# Revit family: NBS_DuPontCorian_CounterTopWashBasins_CorianSingleSink966
name_source: partatom
category: Plumbing Fixtures
revit_build: Autodesk Revit 2014 (Build: 20130709_2115(x64)
units: mm (PartAtom-declared; Revit-internal decimal feet)

## types (1)
- CorianSingleSink966
    AssetType = Fixed
    BIMObjectName = NBS_DuPontCorian_CounterTopWashBasins_CorianSingleSink966
    ColourOptions = Bone, Cameo White, Designer White, Glacier White, Vanilla
    Default Elevation = 0 mm  [stored 0 ft]
    Description = The extraordinary versatility of DuPont™ Corian® makes it the right choice for bathrooms. Bathroom basins made with Corian® combine beauty, functionality, durability and stain resistance with easy care and the abundant design and colour options that make all the difference.
    DrainSize = 0 mm  [stored 0 ft]
    DurationUnit = year
    Features = Designed to be integrated into a Corian® worksurface. Available in full colour range as Standard or bespoke colours. Hygienic.
    Finish = Semi gloss
    Form = Inset countertop or Mounted under countertop (undermount)
    IfcExportAs = IfcSanitaryTerminalType
    IfcExportType = WASHHANDBASIN
    IntegralAccessories = Includes overflow piece and 25mm diameter overflow elbow
    InternalDepth = 176 mm
    InternalLength = 700 mm
    InternalWidth = 401 mm
    Manufacturer = DuPont™ Corian®
    ManufacturerName = DuPont Corian
    ManufacturerURL = www.corian.co.uk
    Material = ±⅓ acrylic resin (also known as polymethyl methacrylate or PMMA) and ±⅔ aluminium trihydrate natural minerals
    ModelNumber = 966
    ModelReference = Corian® Single Sink
    MountingOptions = Undermount classical, Undermount seamless
    NBSCertification = http://www.nationalbimlibrary.com
    NBSDescription = Counter top wash basins
    NBSReference = 45-35-70/360
    Name = Counter top wash basins
    NominalDepth = 191 mm
    NominalHeight = 0 mm  [stored 0 ft]
    NominalLength = 750 mm
    NominalWidth = 451 mm
    ProductInformation = corian.co.uk/Corian/en_GB/assets/downloads/documentation/corian_sinks_bowls_en.pdf
    ReplacementCost = 0.0
    Shape = Rectangular
    Size = 750 x 451 x 191 mm
    SustainabilityPerformance = ISO14001. Zero landfill at manufacturing site. Greenguard certified. Repairable nature makes lifetime performance 40 years plus.
    Uniclass2 = 45-31-79/418
    Version = 3
    WarrantyDescription = 10 year material warranty from DuPont™
    WarrantyDurationParts = 10 years
    WarrantyDurationUnit = year
    WashBasinMaterial = NBS_Concept
    WaterSupplyOverflowAndWasteHoles = No tapholes, rear overflow hole, bottom waste outlet with no chainstay hole

note: [stored X ft] marks values corroborated as IEEE doubles in the binary element streams (Revit-internal decimal feet)

## geometry (parser evidence)
native form markers: Sweep x1
no freeform markers — native parametric forms only
